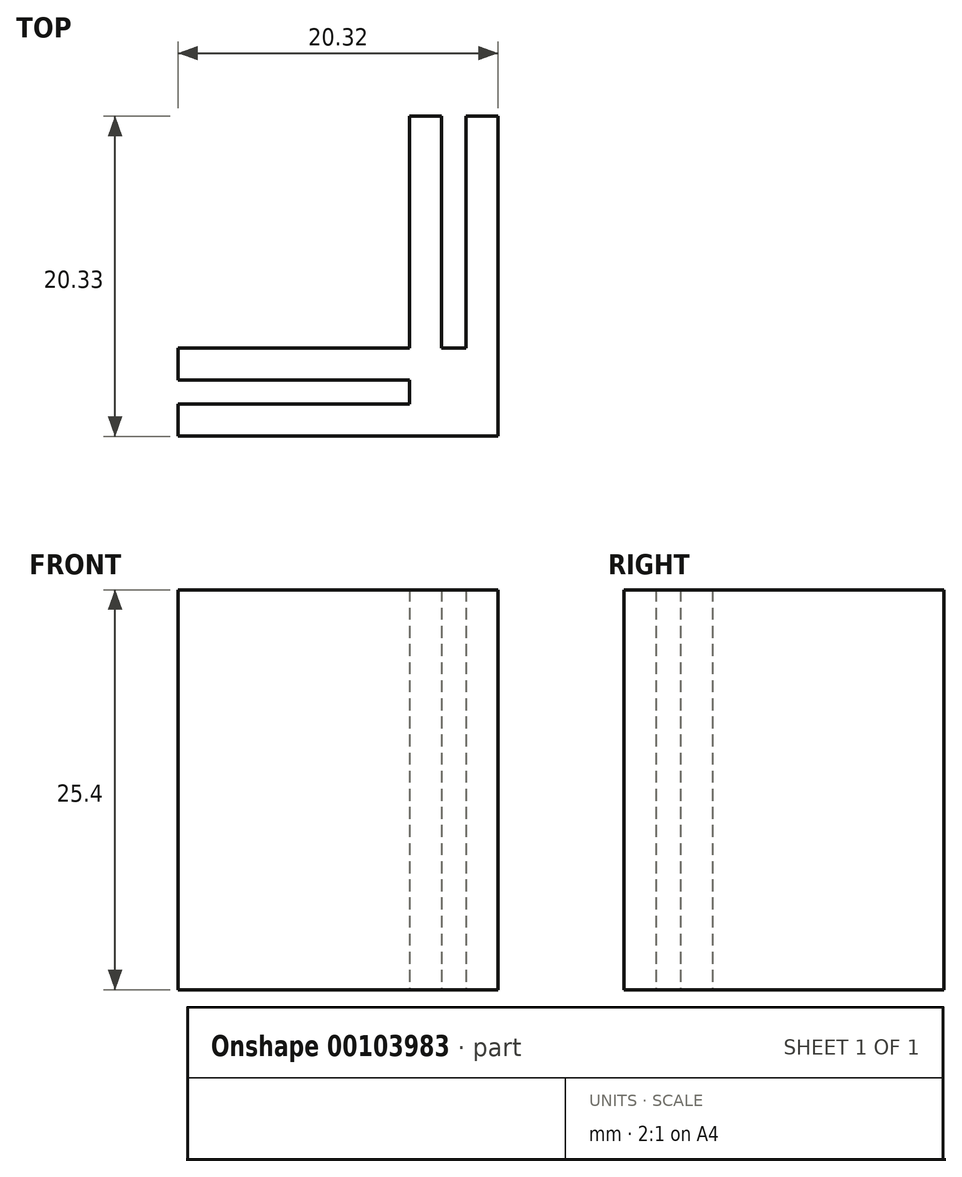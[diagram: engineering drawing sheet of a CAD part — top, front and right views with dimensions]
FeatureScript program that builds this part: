
annotation { "Feature Type Name" : "Feature", "Feature Type Description" : "" }
export const myFeature = defineFeature(function(context is Context, id is Id, definition is map)
    precondition{}
    {
        {
            var Q0;
            Q0=qCreatedBy(makeId("Top.planeOp"),FACE);
            var sketch = newSketch(context, id + "F0", { "sketchPlane" : qUnion([Q0])});
            skLineSegment(sketch, "E0", {"start": v(-59.81, -28.06) * mm, "end": v(-39.49, -28.06) * mm});
            skLineSegment(sketch, "E1", {"start": v(-39.49, -28.06) * mm, "end": v(-39.49, -7.73) * mm});
            skLineSegment(sketch, "E2", {"start": v(-39.49, -7.73) * mm, "end": v(-41.53, -7.73) * mm});
            skLineSegment(sketch, "E3", {"start": v(-41.53, -7.73) * mm, "end": v(-41.53, -22.44) * mm});
            skLineSegment(sketch, "E4", {"start": v(-41.53, -22.44) * mm, "end": v(-43.07, -22.44) * mm});
            skLineSegment(sketch, "E5", {"start": v(-43.07, -22.44) * mm, "end": v(-43.07, -7.73) * mm});
            skLineSegment(sketch, "E6", {"start": v(-43.07, -7.73) * mm, "end": v(-45.1, -7.73) * mm});
            skLineSegment(sketch, "E7", {"start": v(-45.1, -7.73) * mm, "end": v(-45.1, -22.44) * mm});
            skLineSegment(sketch, "E8", {"start": v(-45.1, -22.44) * mm, "end": v(-59.81, -22.44) * mm});
            skLineSegment(sketch, "E9", {"start": v(-59.81, -22.44) * mm, "end": v(-59.81, -24.48) * mm});
            skLineSegment(sketch, "E10", {"start": v(-59.81, -24.48) * mm, "end": v(-45.1, -24.48) * mm});
            skLineSegment(sketch, "E11", {"start": v(-45.1, -24.48) * mm, "end": v(-45.1, -26.02) * mm});
            skLineSegment(sketch, "E12", {"start": v(-45.1, -26.02) * mm, "end": v(-59.81, -26.02) * mm});
            skLineSegment(sketch, "E13", {"start": v(-59.81, -26.02) * mm, "end": v(-59.81, -28.06) * mm});
            skSolve(sketch);
        }
        {
            var Q0;
            Q0 = qSketchRegion(id + "F0", true);
            var Q1;
            Q1=makeQuery(id+"F0.imprint","IMPRINT",FACE,{"disambiguationData":[TD([[makeQuery(id+"F0.imprint","IMPRINT",EDGE,{"derivedFrom":sQuery(id+"F0.wireOp",EDGE,"E0")}),1.0]])]});
            extrude(context, id + "F1", {"entities" : qUnion([Q0, Q1]), "depth" : 25.4 * mm});
        }
    });
